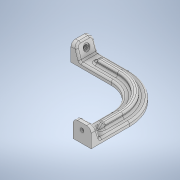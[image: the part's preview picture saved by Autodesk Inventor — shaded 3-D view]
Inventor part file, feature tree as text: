
AUTODESK INVENTOR PART (.ipt)
format: ipt  version: 2021 (Build 250183000, 183)  size: 332,800 bytes
history: native  units: mm
features: sketch x6, extrude x4, fillet x4, projected_geometry x3, plane x2, hole x2, other x1, chamfer x1
ambient origin geometry x8: Origin, YZ Plane, XZ Plane, XY Plane, X Axis, Y Axis, Z Axis, Center Point
bodies: Body1 (feature_tree)
feature tree (23):
  other  "實體1"
  extrude  "擠出1"  Depth=95.0mm
  extrude  "擠出2"  Depth=92.5mm
  plane  "工作平面1"
  hole  "孔1"  [1 undecoded]
  extrude  "擠出3"  Depth=20.0mm
  plane  "工作平面2"
  hole  "孔2"  [1 undecoded]
  fillet  "圓角1"  Radius=15.0mm
  extrude  "擠出5"  Depth=5.0mm
  chamfer  "倒角2"  Distance=10.0mm
  fillet  "圓角2"  Radius=5.0mm
  fillet  "圓角3"  Radius=15.0mm
  fillet  "圓角5"  Radius=5.0mm
  sketch  "草圖1"
  sketch  "草圖2"
  sketch  "草圖3"
  projected_geometry  "投影迴路1"
  sketch  "草圖4"
  sketch  "草圖5"
  projected_geometry  "投影迴路2"
  sketch  "草圖7"
  projected_geometry  "投影迴路4"
note: 2 required parameter values undecoded (feature->parameter linkage not recoverable at this tier; creation-order binding heuristic only, values carry confidence <= 0.55)
